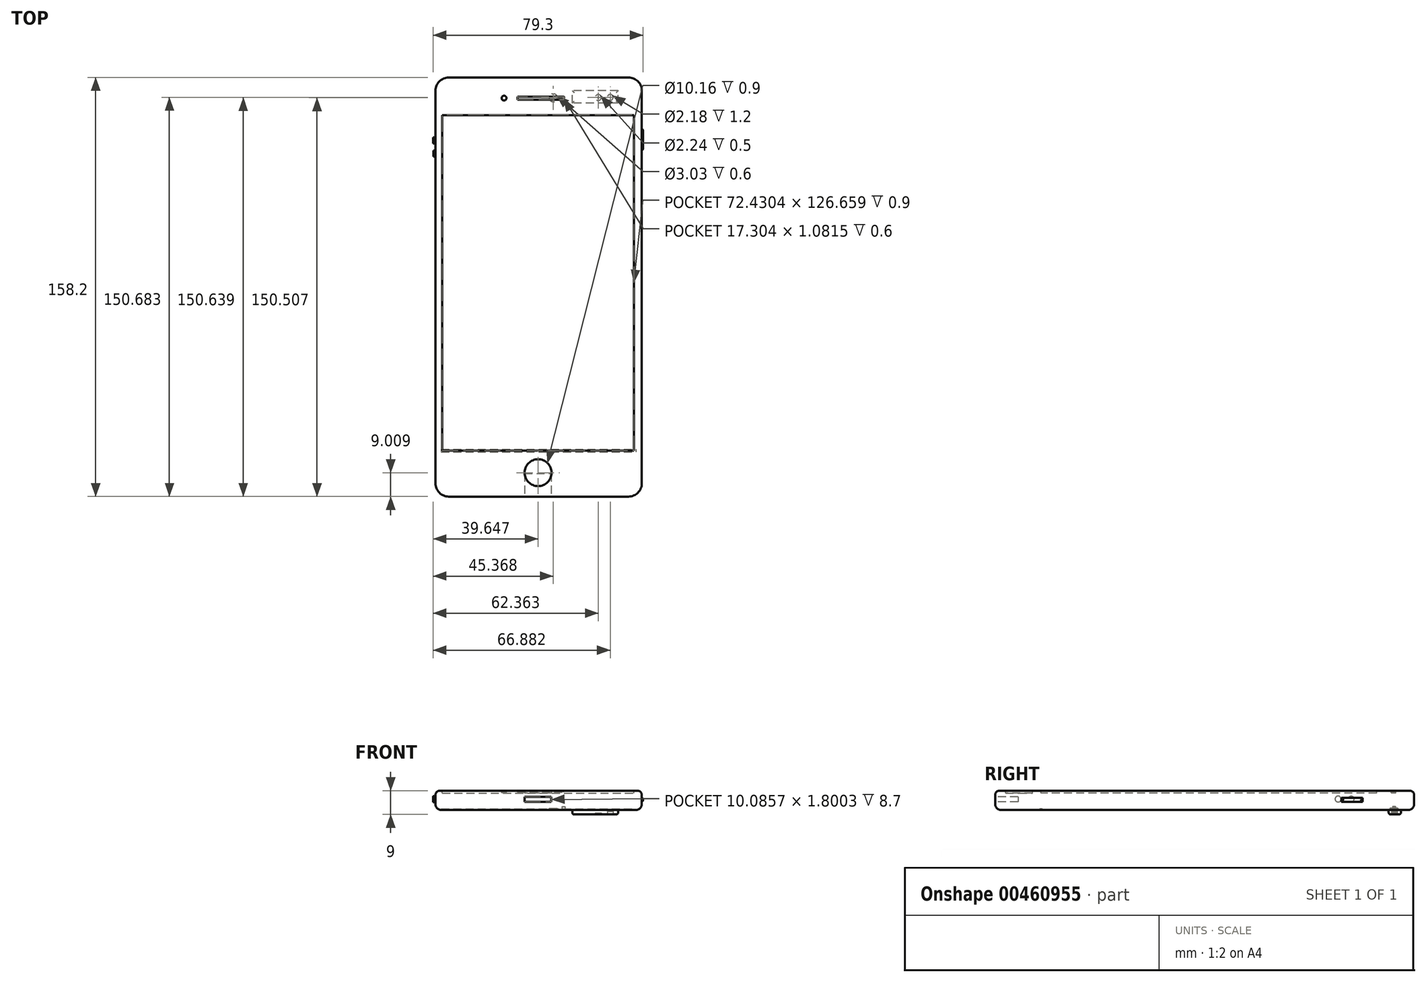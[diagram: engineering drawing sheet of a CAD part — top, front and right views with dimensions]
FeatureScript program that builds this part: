
annotation { "Feature Type Name" : "Feature", "Feature Type Description" : "" }
export const myFeature = defineFeature(function(context is Context, id is Id, definition is map)
    precondition{}
    {
        {
            var Q0;
            Q0=qCreatedBy(makeId("Top.planeOp"),FACE);
            var sketch = newSketch(context, id + "F0", { "sketchPlane" : qUnion([Q0])});
            skLineSegment(sketch, "E0.bottom", {"start": v(-48.33, 65.52) * mm, "end": v(29.57, 65.52) * mm});
            skLineSegment(sketch, "E0.top", {"start": v(-48.33, -92.68) * mm, "end": v(29.57, -92.68) * mm});
            skLineSegment(sketch, "E0.left", {"start": v(-48.33, 65.52) * mm, "end": v(-48.33, -92.68) * mm});
            skLineSegment(sketch, "E0.right", {"start": v(29.57, 65.52) * mm, "end": v(29.57, -92.68) * mm});
            skSolve(sketch);
        }
        {
            var Q0;
            Q0 = qSketchRegion(id + "F0", true);
            extrude(context, id + "F1", {"entities" : qUnion([Q0]), "depth" : 7.3 * mm});
        }
        {
            var Q0;
            Q0=makeQuery(id+"F1.opExtrude","SWEPT_EDGE",EDGE,{"disambiguationData":[OSD([sQuery(id+"F0.wireOp",EDGE,"E0.top"),sQuery(id+"F0.wireOp",EDGE,"E0.left")])]});
            var Q1;
            Q1=makeQuery(id+"F1.opExtrude","SWEPT_EDGE",EDGE,{"disambiguationData":[OSD([sQuery(id+"F0.wireOp",EDGE,"E0.top"),sQuery(id+"F0.wireOp",EDGE,"E0.right")])]});
            var Q2;
            Q2=makeQuery(id+"F1.opExtrude","SWEPT_EDGE",EDGE,{"disambiguationData":[OSD([sQuery(id+"F0.wireOp",EDGE,"E0.bottom"),sQuery(id+"F0.wireOp",EDGE,"E0.right")])]});
            var Q3;
            Q3=makeQuery(id+"F1.opExtrude","SWEPT_EDGE",EDGE,{"disambiguationData":[OSD([sQuery(id+"F0.wireOp",EDGE,"E0.bottom"),sQuery(id+"F0.wireOp",EDGE,"E0.left")])]});
            fillet(context, id + "F2", {"entities" : qUnion([Q0, Q1, Q2, Q3]), "radius" : 5 * mm, "tangentPropagation" : true, "allowEdgeOverflow" : false});
        }
        {
            var Q0;
            Q0=makeQuery(id+"F1.opExtrude","CAP_EDGE",EDGE,{"disambiguationData":[OSD([sQuery(id+"F0.wireOp",EDGE,"E0.left")])],"isStart":false});
            fillet(context, id + "F3", {"entities" : qUnion([Q0]), "radius" : 1.69 * mm, "tangentPropagation" : true, "allowEdgeOverflow" : false});
        }
        {
            var Q0;
            Q0=makeQuery(id+"F1.opExtrude","CAP_EDGE",EDGE,{"disambiguationData":[OSD([sQuery(id+"F0.wireOp",EDGE,"E0.left")])],"isStart":true});
            fillet(context, id + "F4", {"entities" : qUnion([Q0]), "radius" : 2.17 * mm, "tangentPropagation" : true, "allowEdgeOverflow" : false});
        }
        {
            var Q0;
            Q0=makeQuery(id+"F1.opExtrude","CAP_FACE",FACE,{"disambiguationData":[OSD([sQuery(id+"F0.wireOp",EDGE,"E0.bottom"),sQuery(id+"F0.wireOp",EDGE,"E0.top"),sQuery(id+"F0.wireOp",EDGE,"E0.left"),sQuery(id+"F0.wireOp",EDGE,"E0.right")])],"isStart":false});
            var sketch = newSketch(context, id + "F5", { "sketchPlane" : qUnion([Q0])});
            skLineSegment(sketch, "E1.bottom", {"start": v(-45.8, 51.34) * mm, "end": v(26.63, 51.34) * mm});
            skLineSegment(sketch, "E1.top", {"start": v(-45.8, -75.32) * mm, "end": v(26.63, -75.32) * mm});
            skLineSegment(sketch, "E1.left", {"start": v(-45.8, 51.34) * mm, "end": v(-45.8, -75.32) * mm});
            skLineSegment(sketch, "E1.right", {"start": v(26.63, 51.34) * mm, "end": v(26.63, -75.32) * mm});
            skSolve(sketch);
        }
        {
            var Q0;
            Q0 = qSketchRegion(id + "F5", true);
            extrude(context, id + "F6", {"entities" : qUnion([Q0]), "operationType" : NewBodyOperationType.REMOVE, "oppositeDirection" : true, "depth" : 0.9 * mm});
        }
        {
            var Q0;
            Q0=makeQuery(id+"F1.opExtrude","CAP_FACE",FACE,{"disambiguationData":[OSD([sQuery(id+"F0.wireOp",EDGE,"E0.bottom"),sQuery(id+"F0.wireOp",EDGE,"E0.top"),sQuery(id+"F0.wireOp",EDGE,"E0.left"),sQuery(id+"F0.wireOp",EDGE,"E0.right")])],"isStart":false});
            var sketch = newSketch(context, id + "F7", { "sketchPlane" : qUnion([Q0])});
            skCircle(sketch, "E2", {"center": v(-9.58, -83.67) * mm, "radius": 5.08 * mm});
            skPoint(sketch, "E2.centerSnap0", {"position": v(-9.58, -75.32) * mm});
            skSolve(sketch);
        }
        {
            var Q0;
            Q0 = qSketchRegion(id + "F7", true);
            extrude(context, id + "F8", {"entities" : qUnion([Q0]), "operationType" : NewBodyOperationType.REMOVE, "oppositeDirection" : true, "depth" : 0.9 * mm});
        }
        {
            var Q0;
            Q0=makeQuery(id+"F1.opExtrude","CAP_FACE",FACE,{"disambiguationData":[OSD([sQuery(id+"F0.wireOp",EDGE,"E0.bottom"),sQuery(id+"F0.wireOp",EDGE,"E0.top"),sQuery(id+"F0.wireOp",EDGE,"E0.left"),sQuery(id+"F0.wireOp",EDGE,"E0.right")])],"isStart":false});
            var sketch = newSketch(context, id + "F9", { "sketchPlane" : qUnion([Q0])});
            skLineSegment(sketch, "E3.bottom", {"start": v(-17.3, 58.21) * mm, "end": v(0, 58.21) * mm});
            skLineSegment(sketch, "E3.top", {"start": v(-17.3, 57.13) * mm, "end": v(0, 57.13) * mm});
            skLineSegment(sketch, "E3.left", {"start": v(-17.3, 58.21) * mm, "end": v(-17.3, 57.13) * mm});
            skLineSegment(sketch, "E3.right", {"start": v(0, 58.21) * mm, "end": v(0, 57.13) * mm});
            skSolve(sketch);
        }
        {
            var Q0;
            Q0 = qSketchRegion(id + "F9", true);
            extrude(context, id + "F10", {"entities" : qUnion([Q0]), "operationType" : NewBodyOperationType.REMOVE, "oppositeDirection" : true, "depth" : 0.6 * mm});
        }
        {
            var Q0;
            Q0=makeQuery(id+"F1.opExtrude","CAP_FACE",FACE,{"disambiguationData":[OSD([sQuery(id+"F0.wireOp",EDGE,"E0.bottom"),sQuery(id+"F0.wireOp",EDGE,"E0.top"),sQuery(id+"F0.wireOp",EDGE,"E0.left"),sQuery(id+"F0.wireOp",EDGE,"E0.right")])],"isStart":false});
            var sketch = newSketch(context, id + "F11", { "sketchPlane" : qUnion([Q0])});
            skCircle(sketch, "E4", {"center": v(-22.44, 57.73) * mm, "radius": 0.9 * mm});
            skSolve(sketch);
        }
        {
            var Q0;
            Q0 = qSketchRegion(id + "F11", true);
            extrude(context, id + "F12", {"entities" : qUnion([Q0]), "operationType" : NewBodyOperationType.REMOVE, "oppositeDirection" : true, "depth" : 0.8 * mm});
        }
        {
            var Q0;
            Q0=makeQuery(id+"F1.opExtrude","CAP_FACE",FACE,{"disambiguationData":[OSD([sQuery(id+"F0.wireOp",EDGE,"E0.bottom"),sQuery(id+"F0.wireOp",EDGE,"E0.top"),sQuery(id+"F0.wireOp",EDGE,"E0.left"),sQuery(id+"F0.wireOp",EDGE,"E0.right")])],"isStart":true});
            var sketch = newSketch(context, id + "F13", { "sketchPlane" : qUnion([Q0])});
            skLineSegment(sketch, "E5.bottom", {"start": v(20.62, -55.88) * mm, "end": v(3.32, -55.88) * mm});
            skLineSegment(sketch, "E5.top", {"start": v(20.62, -60.52) * mm, "end": v(3.32, -60.52) * mm});
            skLineSegment(sketch, "E5.left", {"start": v(20.62, -55.88) * mm, "end": v(20.62, -60.52) * mm});
            skLineSegment(sketch, "E5.right", {"start": v(3.32, -55.88) * mm, "end": v(3.32, -60.52) * mm});
            skSolve(sketch);
        }
        {
            var Q0;
            Q0 = qSketchRegion(id + "F13", true);
            extrude(context, id + "F14", {"entities" : qUnion([Q0]), "operationType" : NewBodyOperationType.ADD, "depth" : 1.7 * mm});
        }
        {
            var Q0;
            Q0=makeQuery(id+"F14.opExtrude","CAP_EDGE",EDGE,{"disambiguationData":[OSD([sQuery(id+"F13.wireOp",EDGE,"E5.top")])],"isStart":false});
            var Q1;
            Q1=makeQuery(id+"F14.opExtrude","CAP_EDGE",EDGE,{"disambiguationData":[OSD([sQuery(id+"F13.wireOp",EDGE,"E5.bottom")])],"isStart":false});
            var Q2;
            Q2=makeQuery(id+"F14.opExtrude","CAP_EDGE",EDGE,{"disambiguationData":[OSD([sQuery(id+"F13.wireOp",EDGE,"E5.left")])],"isStart":false});
            var Q3;
            Q3=makeQuery(id+"F14.opExtrude","CAP_EDGE",EDGE,{"disambiguationData":[OSD([sQuery(id+"F13.wireOp",EDGE,"E5.right")])],"isStart":false});
            fillet(context, id + "F15", {"entities" : qUnion([Q0, Q1, Q2, Q3]), "radius" : 0.72 * mm, "tangentPropagation" : true, "allowEdgeOverflow" : false});
        }
        {
            var Q0;
            Q0=makeQuery(id+"F14.opExtrude","CAP_FACE",FACE,{"disambiguationData":[OSD([sQuery(id+"F13.wireOp",EDGE,"E5.bottom"),sQuery(id+"F13.wireOp",EDGE,"E5.top"),sQuery(id+"F13.wireOp",EDGE,"E5.left"),sQuery(id+"F13.wireOp",EDGE,"E5.right")])],"isStart":false});
            var sketch = newSketch(context, id + "F16", { "sketchPlane" : qUnion([Q0])});
            skCircle(sketch, "E6", {"center": v(17.65, -58) * mm, "radius": 1.1 * mm});
            skSolve(sketch);
        }
        {
            var Q0;
            Q0 = qSketchRegion(id + "F16", true);
            extrude(context, id + "F17", {"entities" : qUnion([Q0]), "operationType" : NewBodyOperationType.REMOVE, "oppositeDirection" : true, "depth" : 1.2 * mm});
        }
        {
            var Q0;
            Q0=makeQuery(id+"F14.opExtrude","CAP_FACE",FACE,{"disambiguationData":[OSD([sQuery(id+"F13.wireOp",EDGE,"E5.bottom"),sQuery(id+"F13.wireOp",EDGE,"E5.top"),sQuery(id+"F13.wireOp",EDGE,"E5.left"),sQuery(id+"F13.wireOp",EDGE,"E5.right")])],"isStart":false});
            var sketch = newSketch(context, id + "F18", { "sketchPlane" : qUnion([Q0])});
            skCircle(sketch, "E7", {"center": v(13.13, -57.96) * mm, "radius": 1.12 * mm});
            skCircle(sketch, "E8", {"center": v(13.13, -57.96) * mm, "radius": 0.26 * mm});
            skSolve(sketch);
        }
        {
            var Q0;
            Q0 = qSketchRegion(id + "F18", true);
            extrude(context, id + "F19", {"entities" : qUnion([Q0]), "operationType" : NewBodyOperationType.REMOVE, "oppositeDirection" : true, "depth" : 0.5 * mm});
        }
        {
            var Q0;
            Q0=makeQuery(id+"F1.opExtrude","CAP_FACE",FACE,{"disambiguationData":[OSD([sQuery(id+"F0.wireOp",EDGE,"E0.bottom"),sQuery(id+"F0.wireOp",EDGE,"E0.top"),sQuery(id+"F0.wireOp",EDGE,"E0.left"),sQuery(id+"F0.wireOp",EDGE,"E0.right")])],"isStart":true});
            var sketch = newSketch(context, id + "F20", { "sketchPlane" : qUnion([Q0])});
            skCircle(sketch, "E9", {"center": v(0, -57.88) * mm, "radius": 0.57 * mm});
            skSolve(sketch);
        }
        {
            var Q0;
            Q0 = qSketchRegion(id + "F20", true);
            extrude(context, id + "F21", {"entities" : qUnion([Q0]), "operationType" : NewBodyOperationType.REMOVE, "oppositeDirection" : true, "depth" : 1.3 * mm});
        }
        {
            var Q0;
            Q0=makeQuery(id+"F1.opExtrude","CAP_FACE",FACE,{"disambiguationData":[OSD([sQuery(id+"F0.wireOp",EDGE,"E0.bottom"),sQuery(id+"F0.wireOp",EDGE,"E0.top"),sQuery(id+"F0.wireOp",EDGE,"E0.left"),sQuery(id+"F0.wireOp",EDGE,"E0.right")])],"isStart":true});
            var sketch = newSketch(context, id + "F22", { "sketchPlane" : qUnion([Q0])});
            skCircle(sketch, "E10", {"center": v(-3.86, -57.83) * mm, "radius": 1.51 * mm});
            skSolve(sketch);
        }
        {
            var Q0;
            Q0 = qSketchRegion(id + "F22", true);
            extrude(context, id + "F23", {"entities" : qUnion([Q0]), "operationType" : NewBodyOperationType.REMOVE, "oppositeDirection" : true, "depth" : 0.6 * mm});
        }
        {
            var Q0;
            Q0=makeQuery(id+"F1.opExtrude","SWEPT_FACE",FACE,{"disambiguationData":[OSD([sQuery(id+"F0.wireOp",EDGE,"E0.top")])]});
            var sketch = newSketch(context, id + "F24", { "sketchPlane" : qUnion([Q0])});
            skLineSegment(sketch, "E11.bottom", {"start": v(-14.72, 4.9) * mm, "end": v(-4.64, 4.9) * mm});
            skLineSegment(sketch, "E11.top", {"start": v(-14.72, 3.1) * mm, "end": v(-4.64, 3.1) * mm});
            skLineSegment(sketch, "E11.left", {"start": v(-14.72, 4.9) * mm, "end": v(-14.72, 3.1) * mm});
            skLineSegment(sketch, "E11.right", {"start": v(-4.64, 4.9) * mm, "end": v(-4.64, 3.1) * mm});
            skSolve(sketch);
        }
        {
            var Q0;
            Q0 = qSketchRegion(id + "F24", true);
            extrude(context, id + "F25", {"entities" : qUnion([Q0]), "operationType" : NewBodyOperationType.REMOVE, "oppositeDirection" : true, "depth" : 8.7 * mm});
        }
        {
            var Q0;
            Q0=makeQuery(id+"F1.opExtrude","SWEPT_FACE",FACE,{"disambiguationData":[OSD([sQuery(id+"F0.wireOp",EDGE,"E0.right")])]});
            var sketch = newSketch(context, id + "F26", { "sketchPlane" : qUnion([Q0])});
            skLineSegment(sketch, "E12.bottom", {"start": v(46.07, 4.6) * mm, "end": v(38.07, 4.6) * mm});
            skLineSegment(sketch, "E12.top", {"start": v(46.07, 3.1) * mm, "end": v(38.07, 3.1) * mm});
            skLineSegment(sketch, "E12.left", {"start": v(46.07, 4.6) * mm, "end": v(46.07, 3.1) * mm});
            skLineSegment(sketch, "E12.right", {"start": v(38.07, 4.6) * mm, "end": v(38.07, 3.1) * mm});
            skSolve(sketch);
        }
        {
            var Q0;
            Q0 = qSketchRegion(id + "F26", true);
            extrude(context, id + "F27", {"entities" : qUnion([Q0]), "operationType" : NewBodyOperationType.ADD, "depth" : 0.5 * mm});
        }
        {
            var Q0;
            Q0=makeQuery(id+"F27.opExtrude","CAP_EDGE",EDGE,{"disambiguationData":[OSD([sQuery(id+"F26.wireOp",EDGE,"E12.left")])],"isStart":false});
            var Q1;
            Q1=makeQuery(id+"F27.opExtrude","CAP_EDGE",EDGE,{"disambiguationData":[OSD([sQuery(id+"F26.wireOp",EDGE,"E12.bottom")])],"isStart":false});
            var Q2;
            Q2=makeQuery(id+"F27.opExtrude","CAP_EDGE",EDGE,{"disambiguationData":[OSD([sQuery(id+"F26.wireOp",EDGE,"E12.right")])],"isStart":false});
            var Q3;
            Q3=makeQuery(id+"F27.opExtrude","CAP_EDGE",EDGE,{"disambiguationData":[OSD([sQuery(id+"F26.wireOp",EDGE,"E12.top")])],"isStart":false});
            fillet(context, id + "F28", {"entities" : qUnion([Q0, Q1, Q2, Q3]), "radius" : 0.75 * mm, "tangentPropagation" : true, "allowEdgeOverflow" : false});
        }
        {
            var Q0;
            Q0=makeQuery(id+"F1.opExtrude","SWEPT_FACE",FACE,{"disambiguationData":[OSD([sQuery(id+"F0.wireOp",EDGE,"E0.left")])]});
            var sketch = newSketch(context, id + "F29", { "sketchPlane" : qUnion([Q0])});
            skCircle(sketch, "E13", {"center": v(-41.74, 4.07) * mm, "radius": 1.1 * mm});
            skSolve(sketch);
        }
        {
            var Q0;
            Q0 = qSketchRegion(id + "F29", true);
            extrude(context, id + "F30", {"entities" : qUnion([Q0]), "operationType" : NewBodyOperationType.ADD, "depth" : 0.9 * mm});
        }
        {
            var Q0;
            Q0=makeQuery(id+"F1.opExtrude","SWEPT_FACE",FACE,{"disambiguationData":[OSD([sQuery(id+"F0.wireOp",EDGE,"E0.left")])]});
            var sketch = newSketch(context, id + "F31", { "sketchPlane" : qUnion([Q0])});
            skCircle(sketch, "E14", {"center": v(-36.8, 4.12) * mm, "radius": 1.13 * mm});
            skSolve(sketch);
        }
        {
            var Q0;
            Q0 = qSketchRegion(id + "F31", true);
            extrude(context, id + "F32", {"entities" : qUnion([Q0]), "operationType" : NewBodyOperationType.ADD, "depth" : 0.8 * mm});
        }
        {
            var Q0;
            Q0=makeQuery(id+"F1.opExtrude","CAP_FACE",FACE,{"disambiguationData":[OSD([sQuery(id+"F0.wireOp",EDGE,"E0.bottom"),sQuery(id+"F0.wireOp",EDGE,"E0.top"),sQuery(id+"F0.wireOp",EDGE,"E0.left"),sQuery(id+"F0.wireOp",EDGE,"E0.right")])],"isStart":true});
            var sketch = newSketch(context, id + "F33", { "sketchPlane" : qUnion([Q0])});
            skLineSegment(sketch, "E15.bottom", {"start": v(-46.15, 75.9) * mm, "end": v(27.4, 75.9) * mm});
            skLineSegment(sketch, "E15.top", {"start": v(-46.15, 74.81) * mm, "end": v(27.4, 74.81) * mm});
            skLineSegment(sketch, "E15.left", {"start": v(-46.15, 75.9) * mm, "end": v(-46.15, 74.81) * mm});
            skLineSegment(sketch, "E15.right", {"start": v(27.4, 75.9) * mm, "end": v(27.4, 74.81) * mm});
            skSolve(sketch);
        }
        {
            var Q0;
            Q0 = qSketchRegion(id + "F33", true);
            extrude(context, id + "F34", {"entities" : qUnion([Q0]), "operationType" : NewBodyOperationType.REMOVE, "oppositeDirection" : true, "depth" : 0.4 * mm});
        }
    });
